# Revit family: ZETA_Коробка_Клемная_КСМР-20_IP54
name_source: partatom
category: Электрические приборы
units: mm (PartAtom-declared; Revit-internal decimal feet)

## family parameters
Всегда вертикально = Нет
На основе рабочей плоскости = Да
Общий = Нет
При загрузке вырезать с полостями = Нет
Размер круглого соединителя = Использовать диаметр
Сохранять ориентацию аннотаций = Нет
Тип детали = Нормальный
Точка принадлежности помещению = Да

## types (2) — shared parameters
ADSK_URL документации изделия = https://nzeta.ru
ADSK_URL страницы изделия = https://nzeta.ru
ADSK_Версия Revit = 2021
ADSK_Версия семейства = v.1
ADSK_Единица измерения = шт
ADSK_Завод-изготовитель = АО «ЗЭТА»
ADSK_Классификация нагрузок = Прочее
ADSK_Код изделия = zeta30375
ADSK_Количество = 1
ADSK_Количество фаз = 1
ADSK_Количество фаз числовое = 1
ADSK_Коэффициент мощности = 1
ADSK_Марка = КК КСМР-20 У2 IP54
ADSK_Масса = 2.4
ADSK_Масса_Текст = 2,4
ADSK_Материал наименование = Сталь оцинкованная
ADSK_Наименование = Коробка соединительная КСМР-20 У2 IP54 ГОФРОМАТИК
ADSK_Наименование краткое = КСМР-20
ADSK_Напряжение = 230 В
ADSK_Номинальная мощность = 0 Вт
ADSK_Обозначение = KK
ADSK_Полная мощность = 0 В·А
ADSK_Размер_Высота = 100 мм
ADSK_Размер_Длина = 336 мм
ADSK_Размер_Ширина = 175 мм
ADSK_Степень защиты_IP = IP54
ADSK_Ток = 0 А
D1 = 25 мм
D2 = 32 мм
D3 = 20 мм
URL = https://nzeta.ru
Изготавливается по = ТУ 27.33.13.120-047-99856433-2020
Изготовитель = АО «ЗЭТА»
Климатическое исполнение = У2
Крышка_Длина = 190 мм
Крышка_Ширина = 160 мм
Напряжение переменного тока = 660 В
Напряжение постоянного тока = 440 В
Номинальный ток = до 25A
Описание = Коробки клеммные КСМР с наборными зажимами применяются для соединения
и разветвления вторичных и силовых цепей, выполняемых контрольными кабелями
с числом жил до 52 и силовыми кабелями с алюминиевыми или медными жилами
сечением 1,5—4 мм2, проложенные в гибких металлорукавах трубной системы
прокладки кабелей по ГОСТ Р МЭК 61386.1-2014.
Отметка по умолчанию = 1219 мм
Сертификат = RU C-RU.АД84.В.00192/20
Сечение жил до = 4мм2
Температура эксплуатации = от -40°С до +60°С
УГО_Высота = 5 мм
УГО_Ширина = 10 мм
zero-valued in all types: ADSK_Номер линии

## type names (no varying parameters)
- КСРМ-20
- КСРМ-20_IP54

## geometry (parser evidence)
native form markers: Sweep x1
no freeform markers — native parametric forms only
